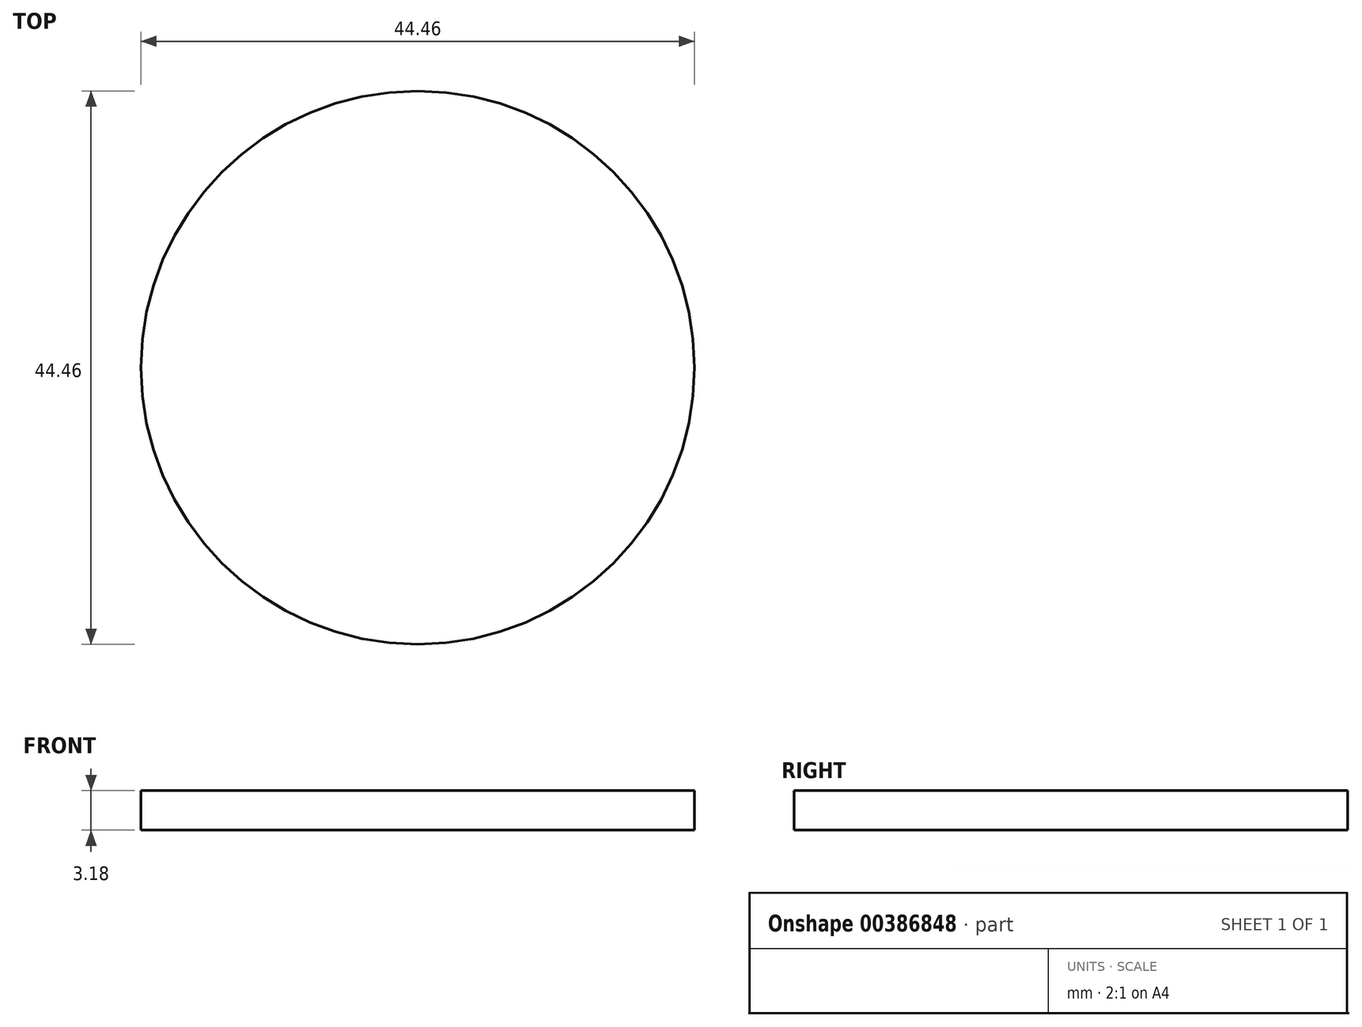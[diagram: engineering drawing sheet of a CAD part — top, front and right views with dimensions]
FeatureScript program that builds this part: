
annotation { "Feature Type Name" : "Feature", "Feature Type Description" : "" }
export const myFeature = defineFeature(function(context is Context, id is Id, definition is map)
    precondition{}
    {
        {
            var Q0;
            Q0=qCreatedBy(makeId("Top.planeOp"),FACE);
            var sketch = newSketch(context, id + "F0", { "sketchPlane" : qUnion([Q0])});
            skCircle(sketch, "E0", {"center": v(0, 0) * mm, "radius": 22.23 * mm});
            skCircle(sketch, "E1", {"center": v(0, 0) * mm, "radius": 19.05 * mm});
            skPoint(sketch, "E2", {"position": v(4.27, 0.76) * mm});
            skPoint(sketch, "E3", {"position": v(4.27, 0) * mm});
            skSolve(sketch);
        }
        {
            var Q0;
            Q0 = qSketchRegion(id + "F0", true);
            var Q1;
            Q1=makeQuery(id+"F0.imprint","IMPRINT",FACE,{"disambiguationData":[TD([[makeQuery(id+"F0.imprint","IMPRINT",EDGE,{"derivedFrom":sQuery(id+"F0.wireOp",EDGE,"E1")}),1.0]])]});
            extrude(context, id + "F1", {"entities" : qUnion([Q0, Q1]), "oppositeDirection" : true, "depth" : 3.17 * mm});
        }
    });
